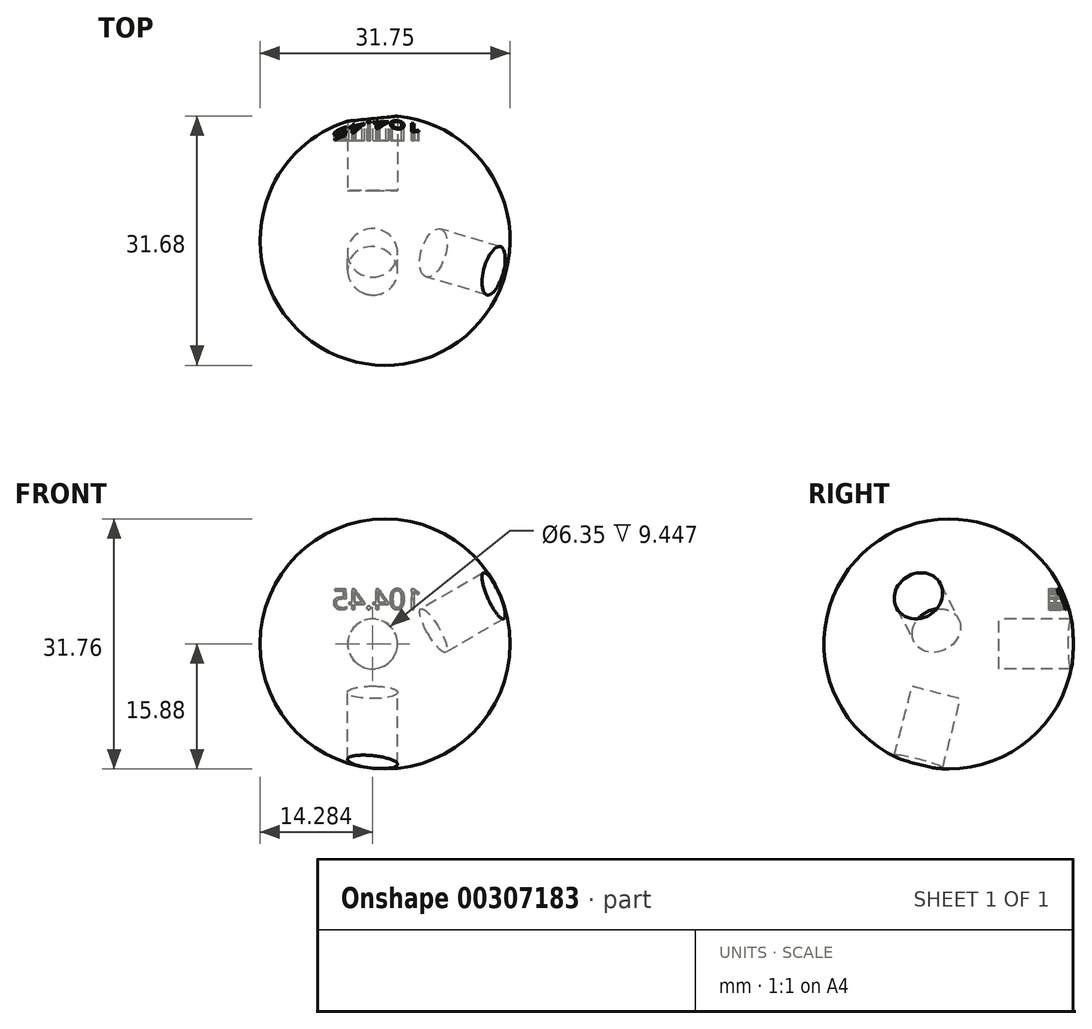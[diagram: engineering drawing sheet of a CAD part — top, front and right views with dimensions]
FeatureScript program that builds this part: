
annotation { "Feature Type Name" : "Feature", "Feature Type Description" : "" }
export const myFeature = defineFeature(function(context is Context, id is Id, definition is map)
    precondition{}
    {
        {
            var Q0;
            Q0=qCreatedBy(makeId("Top.planeOp"),FACE);
            var sketch = newSketch(context, id + "F0", { "sketchPlane" : qUnion([Q0])});
            skCircle(sketch, "E0", {"center": v(0, 0) * mm, "radius": 15.88 * mm});
            skSolve(sketch);
        }
        {
            var Q0;
            Q0=qCreatedBy(makeId("Front.planeOp"),FACE);
            var sketch = newSketch(context, id + "F1", { "sketchPlane" : qUnion([Q0])});
            skArc(sketch, "E1", {"start": v(0, 15.88) * mm, "mid": v(-15.88, 0) * mm, "end": v(0, -15.88) * mm});
            skLineSegment(sketch, "E2", {"start": v(0, -15.88) * mm, "end": v(0, 15.88) * mm});
            skSolve(sketch);
        }
        {
            var Q0;
            Q0=qSketchRegion(id+"F1",true);
            var Q1;
            Q1=sQuery(id+"F0.wireOp",EDGE,"E0");
            revolve(context, id + "F2", {"entities" : qUnion([Q0]), "axis" : qUnion([Q1]), "revolveType" : RevolveType.FULL});
        }
        {
            var Q0;
            Q0=qCreatedBy(makeId("Front.planeOp"),FACE);
            cPlane(context, id + "F3", {"entities" : qUnion([Q0]), "cplaneType" : CPlaneType.OFFSET, "offset" : 6.35 * mm, "oppositeDirection" : true, "width" : 152.4 * mm, "height" : 152.4 * mm});
        }
        {
            var Q0;
            Q0=qCreatedBy(id+"F3.planeOp",FACE);
            var sketch = newSketch(context, id + "F4", { "sketchPlane" : qUnion([Q0])});
            skCircle(sketch, "E3", {"center": v(-1.6, 0) * mm, "radius": 3.18 * mm});
            skSolve(sketch);
        }
        {
            var Q0;
            Q0=qSketchRegion(id+"F4",true);
            extrude(context, id + "F5", {"entities" : qUnion([Q0]), "oppositeDirection" : true, "depth" : 38.1 * mm});
        }
        {
            var Q0;
            Q0=makeQuery(id+"F5.opExtrude","CAP_FACE",FACE,{"disambiguationData":[OSD([sQuery(id+"F4.wireOp",EDGE,"E3")])],"isStart":false});
            var sketch = newSketch(context, id + "F6", { "sketchPlane" : qUnion([Q0])});
            skText(sketch, "E4", { "text": "104.45", "fontName": "OpenSans-Regular.ttf"});
            const initialGuessF6  = {"E4": [-0.00465, 0.00439, 1, 0, 0.00262]};
            skSetInitialGuess(sketch, initialGuessF6);
            skSolve(sketch);
        }
        {
            var Q0;
            Q0=qSketchRegion(id+"F6",true);
            extrude(context, id + "F7", {"entities" : qUnion([Q0]), "operationType" : NewBodyOperationType.REMOVE, "oppositeDirection" : true, "depth" : 31.75 * mm});
        }
        {
            var Q0;
            Q0=qCreatedBy(makeId("Front.planeOp"),FACE);
            var sketch = newSketch(context, id + "F8", { "sketchPlane" : qUnion([Q0])});
            skLineSegment(sketch, "E5", {"start": v(0, 0) * mm, "end": v(0, 31.16) * mm, "construction": true});
            skLineSegment(sketch, "E6", {"start": v(0, 0) * mm, "end": v(39.64, 0) * mm, "construction": true});
            skLineSegment(sketch, "E7", {"start": v(0, 0) * mm, "end": v(-35.4, 0) * mm, "construction": true});
            skSolve(sketch);
        }
        {
            var Q0;
            Q0=qCreatedBy(makeId("Right.planeOp"),FACE);
            var sketch = newSketch(context, id + "F9", { "sketchPlane" : qUnion([Q0])});
            skLineSegment(sketch, "E8", {"start": v(0, 0) * mm, "end": v(-40.37, 0) * mm, "construction": true});
            skLineSegment(sketch, "E9", {"start": v(0, 0) * mm, "end": v(0, -35.95) * mm, "construction": true});
            skSolve(sketch);
        }
        {
            var Q0;
            Q0=makeQuery(id+"F5.opExtrude","SWEPT_BODY",BODY,{"disambiguationData":[OSD([sQuery(id+"F4.wireOp",EDGE,"E3")])]});
            var Q1;
            Q1=sQuery(id+"F8.wireOp",EDGE,"E6");
            transform(context, id + "F10", {"entities" : qUnion([Q0]), "transformType" : TransformType.ROTATION, "transformAxis" : qUnion([Q1]), "angle" : 104.45 * degree, "oppositeDirection" : true, "makeCopy" : true});
        }
        {
            var Q0;
            Q0=makeQuery(id+"F10.opPattern","COPY",BODY,{"derivedFrom":makeQuery(id+"F5.opExtrude","SWEPT_BODY",BODY,{"disambiguationData":[OSD([sQuery(id+"F4.wireOp",EDGE,"E3")])]}),"instanceName":"1"});
            var Q1;
            Q1=sQuery(id+"F9.wireOp",EDGE,"E8");
            transform(context, id + "F11", {"entities" : qUnion([Q0]), "transformType" : TransformType.ROTATION, "transformAxis" : qUnion([Q1]), "angle" : 120 * degree, "makeCopy" : true});
        }
        {
            var Q0;
            Q0=makeQuery(id+"F11.opPattern","COPY",BODY,{"derivedFrom":makeQuery(id+"F10.opPattern","COPY",BODY,{"derivedFrom":makeQuery(id+"F5.opExtrude","SWEPT_BODY",BODY,{"disambiguationData":[OSD([sQuery(id+"F4.wireOp",EDGE,"E3")])]}),"instanceName":"1"}),"instanceName":"1"});
            var Q1;
            Q1=makeQuery(id+"F10.opPattern","COPY",BODY,{"derivedFrom":makeQuery(id+"F5.opExtrude","SWEPT_BODY",BODY,{"disambiguationData":[OSD([sQuery(id+"F4.wireOp",EDGE,"E3")])]}),"instanceName":"1"});
            var Q2;
            Q2=makeQuery(id+"F5.opExtrude","SWEPT_BODY",BODY,{"disambiguationData":[OSD([sQuery(id+"F4.wireOp",EDGE,"E3")])]});
            var Q3;
            Q3=makeQuery(id+"F2.opRevolve","SWEPT_BODY",BODY,{"disambiguationData":[OSD([sQuery(id+"F1.wireOp",EDGE,"E1"),sQuery(id+"F1.wireOp",EDGE,"E2")])]});
            booleanBodies(context, id + "F12", {"operationType" : BooleanOperationType.SUBTRACTION, "tools" : qUnion([Q0, Q1, Q2]), "targets" : qUnion([Q3])});
        }
    });
